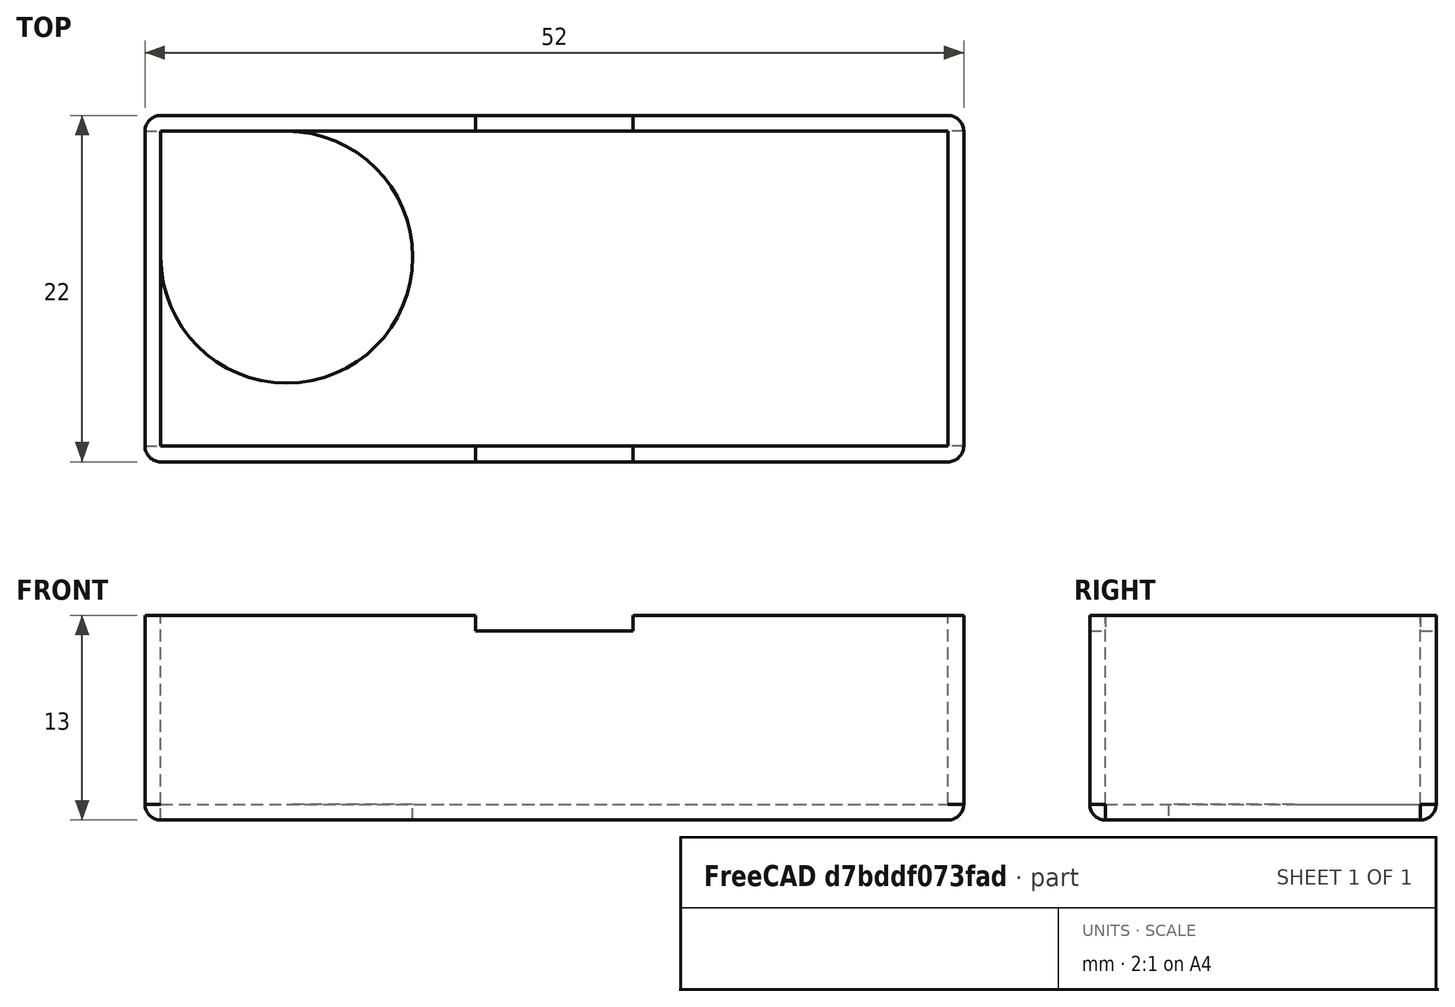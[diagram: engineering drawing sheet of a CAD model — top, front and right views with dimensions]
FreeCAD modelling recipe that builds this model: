
FCSTD DOCUMENT  (FreeCAD 0.21R33771 (Git))
Label: case
License: All rights reserved
LicenseURL: http://en.wikipedia.org/wiki/All_rights_reserved
objects: PartDesign::SubtractiveBox×2, PartDesign::AdditiveBox×1, PartDesign::Thickness×1, PartDesign::SubtractiveCylinder×1, PartDesign::Body×1
note: 11 computed .brp shape members not serialized (recipe doc carries the construction recipe); baked Part::Feature solids carry a one-line shape summary decoded from their .brp

FEATURE [PartDesign::AdditiveBox] Box
  AttacherType = Attacher::AttachEngine3D
  Height = 12
  Length = 50
  Width = 20
FEATURE [PartDesign::Thickness] Thickness
  Base = -> Box [Face6]
  BaseFeature = -> Box
  Intersection = false
  Join = 0
  Mode = 0
  SupportTransform = false
  Value = 1
FEATURE [PartDesign::SubtractiveCylinder] Cylinder
  Angle = 360
  AttacherType = Attacher::AttachEngine3D
  AttachmentOffset = pos=(8,12,-1) rot=(0,0,1;0rad)
  BaseFeature = -> Thickness
  FirstAngle = 0
  Height = 1
  MapMode = 2
  Placement = pos=(8,12,-1) rot=(0,0,1;0rad)
  Radius = 8
  SecondAngle = 0
  Support = -> [Thickness]
FEATURE [PartDesign::SubtractiveBox] Box001
  AttacherType = Attacher::AttachEngine3D
  AttachmentOffset = pos=(12,-13,-1) rot=(0,0,1;0rad)
  BaseFeature = -> Cylinder
  Height = 1
  Length = 10
  MapMode = 5
  Placement = pos=(20,-1,11) rot=(0,0,1;0rad)
  Support = -> [Cylinder]
  Width = 22
FEATURE [PartDesign::SubtractiveBox] Box002
  AttacherType = Attacher::AttachEngine3D
  AttachmentOffset = pos=(-20,13,-1) rot=(0,0,1;0rad)
  BaseFeature = -> Box001
  Height = 1
  Length = 8
  MapMode = 5
  Placement = pos=(0,12,-1) rot=(0,0,1;0rad)
  Support = -> [Box001]
  Width = 8
FEATURE [PartDesign::Body] Body
  Group = -> [Box,Thickness,Cylinder,Box001,Box002]
  Origin = -> Origin
  Tip = -> Box002
